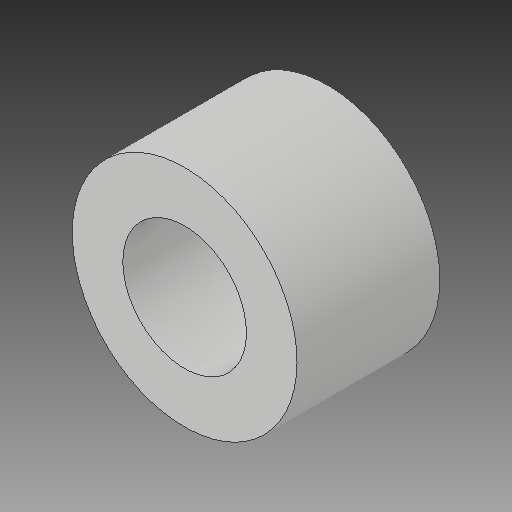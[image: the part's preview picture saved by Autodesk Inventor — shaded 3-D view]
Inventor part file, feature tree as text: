
AUTODESK INVENTOR PART (.ipt)
format: ipt  version: 2017 (Build 210142000, 142)  size: 101,376 bytes
history: native  units: mm
features: other x3, sketch x1
ambient origin geometry x8: Origin, YZ Plane, XZ Plane, XY Plane, X Axis, Y Axis, Z Axis, Center Point
bodies: Solid1 (feature_tree)
feature tree (4):
  other  "Small-Aluminium-Spacer.ipt"
  other  "Solid1::Small-Aluminium-Spacer.ipt"
  other  "TaggingFeature1"
  sketch  "Sketch1"  dims[d0=10.0mm]
